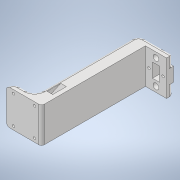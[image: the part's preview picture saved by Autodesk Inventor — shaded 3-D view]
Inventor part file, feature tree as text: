
AUTODESK INVENTOR PART (.ipt)
format: ipt  version: 2022.3 (Build 263350000, 350)  size: 428,032 bytes
history: native  units: mm
features: sketch x13, extrude x7, fillet x5, hole x2, sweep x2, emboss x1
ambient origin geometry x8: Origin, YZ Plane, XZ Plane, XY Plane, X Axis, Y Axis, Z Axis, Center Point
bodies: Solid1 (feature_tree)
feature tree (30):
  extrude  "Extrusion1"  Depth=20.0mm
  fillet  "Fillet1"  Radius=50.0mm
  extrude  "Extrusion8"  Depth=40.0mm
  fillet  "Fillet2"  Radius=10.0mm
  fillet  "Fillet3"  Radius=50.0mm
  extrude  "Extrusion2"  Depth=5.0mm
  hole  "Hole1"  [1 undecoded]
  sweep  "Sweep1"
  sweep  "Sweep2"
  sketch  "Sketch8"  dims[d18=5.0mm d19=3.4mm]
  extrude  "Extrusion3"  Depth=40.0mm
  extrude  "Extrusion4"  Depth=3.4mm
  extrude  "Extrusion5"  Depth=3.4mm
  fillet  "Fillet5"  Radius=3.4mm
  emboss  "Emboss1"
  hole  "Hole4"  [1 undecoded]
  fillet  "Fillet7"  Radius=8.0mm
  extrude  "Extrusion9"  Depth=20.0mm
  sketch  "Sketch1"  dims[d0=20.0mm d1=148.0mm d2=50.0mm]
  sketch  "Sketch2"  dims[d3=10.0mm d4=40.0mm d5=10.0mm d6=50.0mm d7=0.0mm]
  sketch  "Sketch3"  dims[d8=10.0mm d9=5.0mm]
  sketch  "Sketch4"  dims[d10=10.0mm d11=10.0mm]
  sketch  "Sketch5"  dims[d12=5.0mm d13=10.0mm]
  sketch  "Sketch6"  dims[d14=5.0mm d15=40.0mm]
  sketch  "Sketch7"  dims[d16=5.0mm d17=40.0mm]
  sketch  "Sketch9"  dims[d20=3.4mm d21=3.4mm d22=3.4mm]
  sketch  "Sketch12"  dims[d23=50.0mm d24=0.0mm]
  sketch  "Sketch13"  dims[d25=3.4mm d26=6.0mm d27=6.0mm d28=2.0mm d29=90.0deg d30=2.2mm d31=0.0mm d32=8.0mm d33=8.0mm]
  sketch  "Sketch16"  dims[d34=20.0mm d35=5.0mm]
  sketch  "Sketch17"  dims[d36=20.0mm d37=9.0mm d38=0.0mm d39=0.0mm d40=0.0mm d41=0.0mm d42=8.0mm d43=8.0mm d44=20.0mm d45=5.0mm d46=20.0mm d47=9.0mm d48=0.0mm d49=0.0mm d50=10.0mm d51=20.0mm d52=8.2mm d53=8.2mm d54=5.0mm d55=0.0mm d56=0.0mm d57=0.0mm d58=12.0mm d59=12.0mm d60=2.0mm d61=0.0mm d77=4.0mm d78=128.0mm d79=40.0mm d80=0.0mm d81=0.0mm d82=1.0mm d83=0.0mm d85=5.0mm d86=5.0mm d87=3.4mm d88=6.0mm d89=4.1mm d90=5.1mm d91=90.0deg d92=0.9mm d93=0.0mm d102=20.0mm d103=10.0mm d104=10.0mm d105=10.0mm d106=50.0mm d107=0.0mm d108=6.0mm d109=2.0mm d110=50.0mm d111=0.0mm d76=0.0mm]
note: 2 required parameter values undecoded (feature->parameter linkage not recoverable at this tier; creation-order binding heuristic only, values carry confidence <= 0.55)
